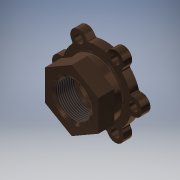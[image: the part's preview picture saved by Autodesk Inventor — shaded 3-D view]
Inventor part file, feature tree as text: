
AUTODESK INVENTOR PART (.ipt)
format: ipt  version: 2018 (Build 220112000, 112)  size: 302,592 bytes
history: native  units: mm (DEFAULTED — no unit token found)
features: sketch x4, fillet x2, extrude x2, revolve x1, thread x1, hole x1, pattern_circular x1
ambient origin geometry x8: Origin, YZ Plane, XZ Plane, XY Plane, X Axis, Y Axis, Z Axis, Center Point
bodies: Solid1 (feature_tree)
feature tree (12):
  revolve  "Revolution1"  [1 undecoded]
  fillet  "Fillet1"  Radius=38.0mm
  extrude  "Extrusion1"  Depth=57.0mm
  thread  "Thread1"  [1 undecoded]
  extrude  "Extrusion2"  Depth=57.0mm
  fillet  "Fillet2"  Radius=5.0mm
  hole  "Hole1"  [1 undecoded]
  pattern_circular  "Circular Pattern1"  [2 undecoded]
  sketch  "Sketch1"  dims[d0=3.0mm d1=32.0mm d2=38.0mm]
  sketch  "Sketch2"  dims[d3=57.0mm d4=40.0mm d5=51.0mm]
  sketch  "Sketch3"  dims[d6=57.0mm d7=74.0mm d8=5.0mm]
  sketch  "Sketch4"  dims[d9=2.0mm d10=21.0mm d11=23.0mm d12=26.0mm d13=29.0mm d14=27.0mm d15=33.0mm d16=36.0mm d17=39.0mm d18=90.0deg d19=2.0mm d20=17.0mm d21=0.0mm d22=10.0mm d23=0.0mm d24=9.0mm d25=78.0mm d26=9.0mm d27=0.0mm d28=2.0mm d29=9.0mm d30=6.0mm d31=4.0mm d32=2.0mm d33=14.3117mm d34=8.0mm d35=20.594885mm d36=60.0mm d38=360.0deg]
note: 5 required parameter values undecoded (feature->parameter linkage not recoverable at this tier; creation-order binding heuristic only, values carry confidence <= 0.55)